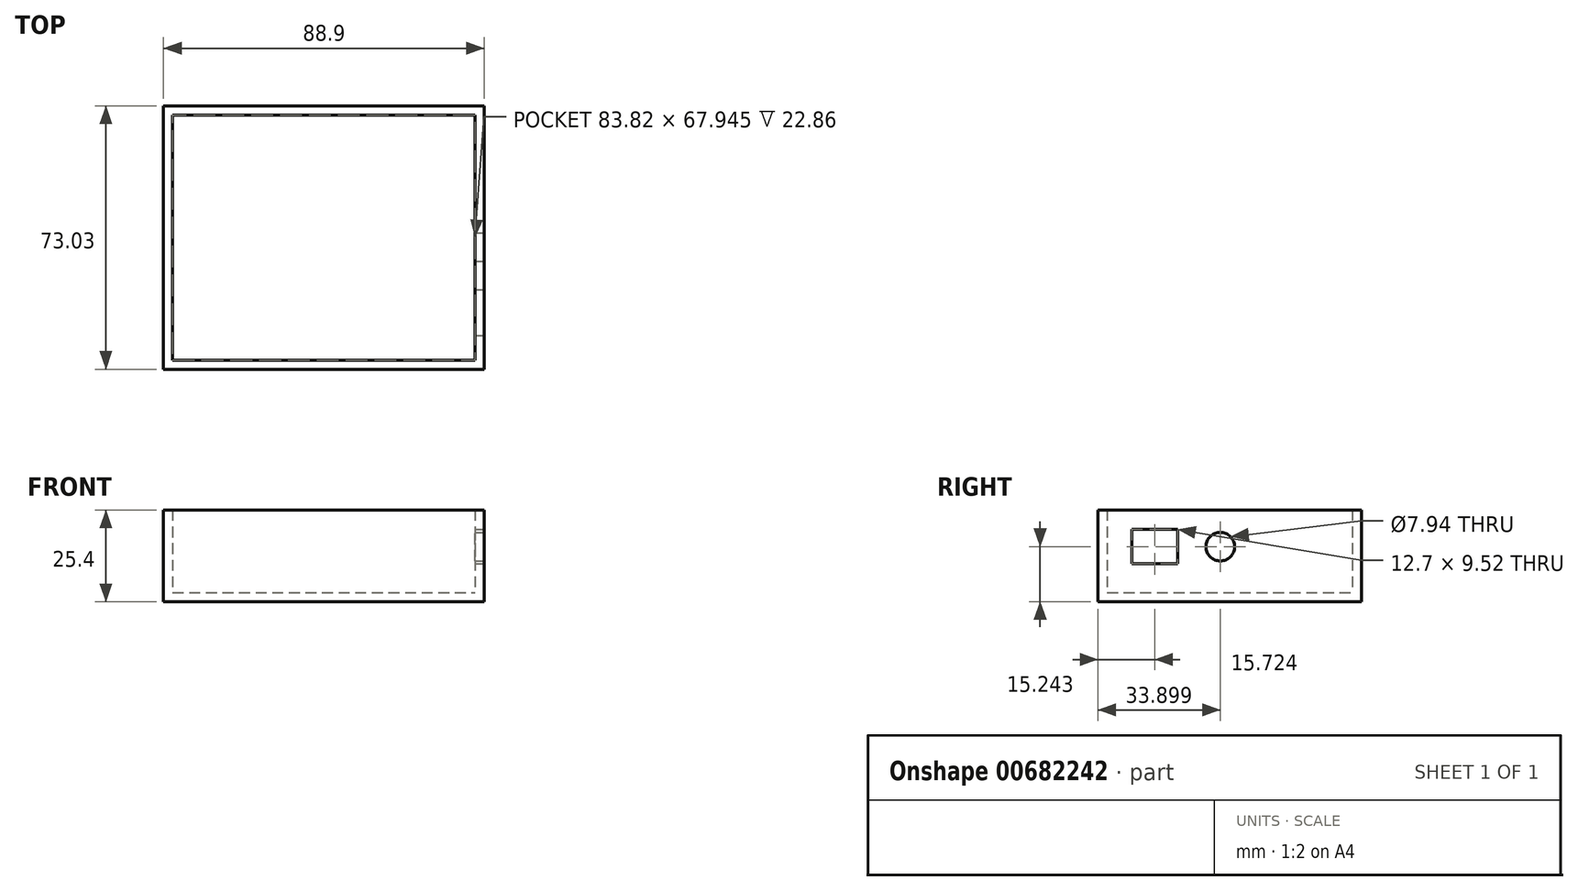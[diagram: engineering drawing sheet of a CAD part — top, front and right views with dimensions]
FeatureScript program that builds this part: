
annotation { "Feature Type Name" : "Feature", "Feature Type Description" : "" }
export const myFeature = defineFeature(function(context is Context, id is Id, definition is map)
    precondition{}
    {
        {
            var Q0;
            Q0=qCreatedBy(makeId("Top.planeOp"),FACE);
            var sketch = newSketch(context, id + "F0", { "sketchPlane" : qUnion([Q0])});
            skLineSegment(sketch, "E0", {"start": v(0, 0) * mm, "end": v(88.9, 0) * mm});
            skLineSegment(sketch, "E1", {"start": v(88.9, 0) * mm, "end": v(88.9, 73.03) * mm});
            skLineSegment(sketch, "E2", {"start": v(88.9, 73.03) * mm, "end": v(0, 73.03) * mm});
            skLineSegment(sketch, "E3", {"start": v(0, 73.03) * mm, "end": v(0, 0) * mm});
            skSolve(sketch);
        }
        {
            var Q0;
            Q0=makeQuery(id+"F0.imprint","IMPRINT",FACE,{"disambiguationData":[TD([[makeQuery(id+"F0.imprint","IMPRINT",EDGE,{"derivedFrom":sQuery(id+"F0.wireOp",EDGE,"E0")}),1.0]])]});
            extrude(context, id + "F1", {"entities" : qUnion([Q0]), "depth" : 25.4 * mm, "offsetDistance" : 25.4 * mm});
        }
        {
            var Q0;
            Q0=makeQuery(id+"F1.opExtrude","CAP_FACE",FACE,{"disambiguationData":[OSD([sQuery(id+"F0.wireOp",EDGE,"E0"),sQuery(id+"F0.wireOp",EDGE,"E1"),sQuery(id+"F0.wireOp",EDGE,"E2"),sQuery(id+"F0.wireOp",EDGE,"E3")])],"isStart":false});
            shell(context, id + "F2", {"entities" : qUnion([Q0]), "thickness" : 2.54 * mm});
        }
        {
            var Q0;
            Q0=makeQuery(id+"F1.opExtrude","SWEPT_FACE",FACE,{"disambiguationData":[OSD([sQuery(id+"F0.wireOp",EDGE,"E1")])]});
            var sketch = newSketch(context, id + "F3", { "sketchPlane" : qUnion([Q0])});
            skLineSegment(sketch, "E4.bottom", {"start": v(22.07, 20) * mm, "end": v(9.37, 20) * mm});
            skLineSegment(sketch, "E4.top", {"start": v(22.07, 10.48) * mm, "end": v(9.37, 10.48) * mm});
            skLineSegment(sketch, "E4.left", {"start": v(22.07, 20) * mm, "end": v(22.07, 10.48) * mm});
            skLineSegment(sketch, "E4.right", {"start": v(9.37, 20) * mm, "end": v(9.37, 10.48) * mm});
            skPoint(sketch, "E4.middle", {"position": v(15.72, 15.24) * mm});
            skCircle(sketch, "E5", {"center": v(33.9, 15.24) * mm, "radius": 3.97 * mm});
            skSolve(sketch);
        }
        {
            var Q0;
            Q0 = qSketchRegion(id + "F3", true);
            extrude(context, id + "F4", {"entities" : qUnion([Q0]), "operationType" : NewBodyOperationType.REMOVE, "oppositeDirection" : true, "depth" : 2.54 * mm, "offsetDistance" : 25.4 * mm});
        }
    });
